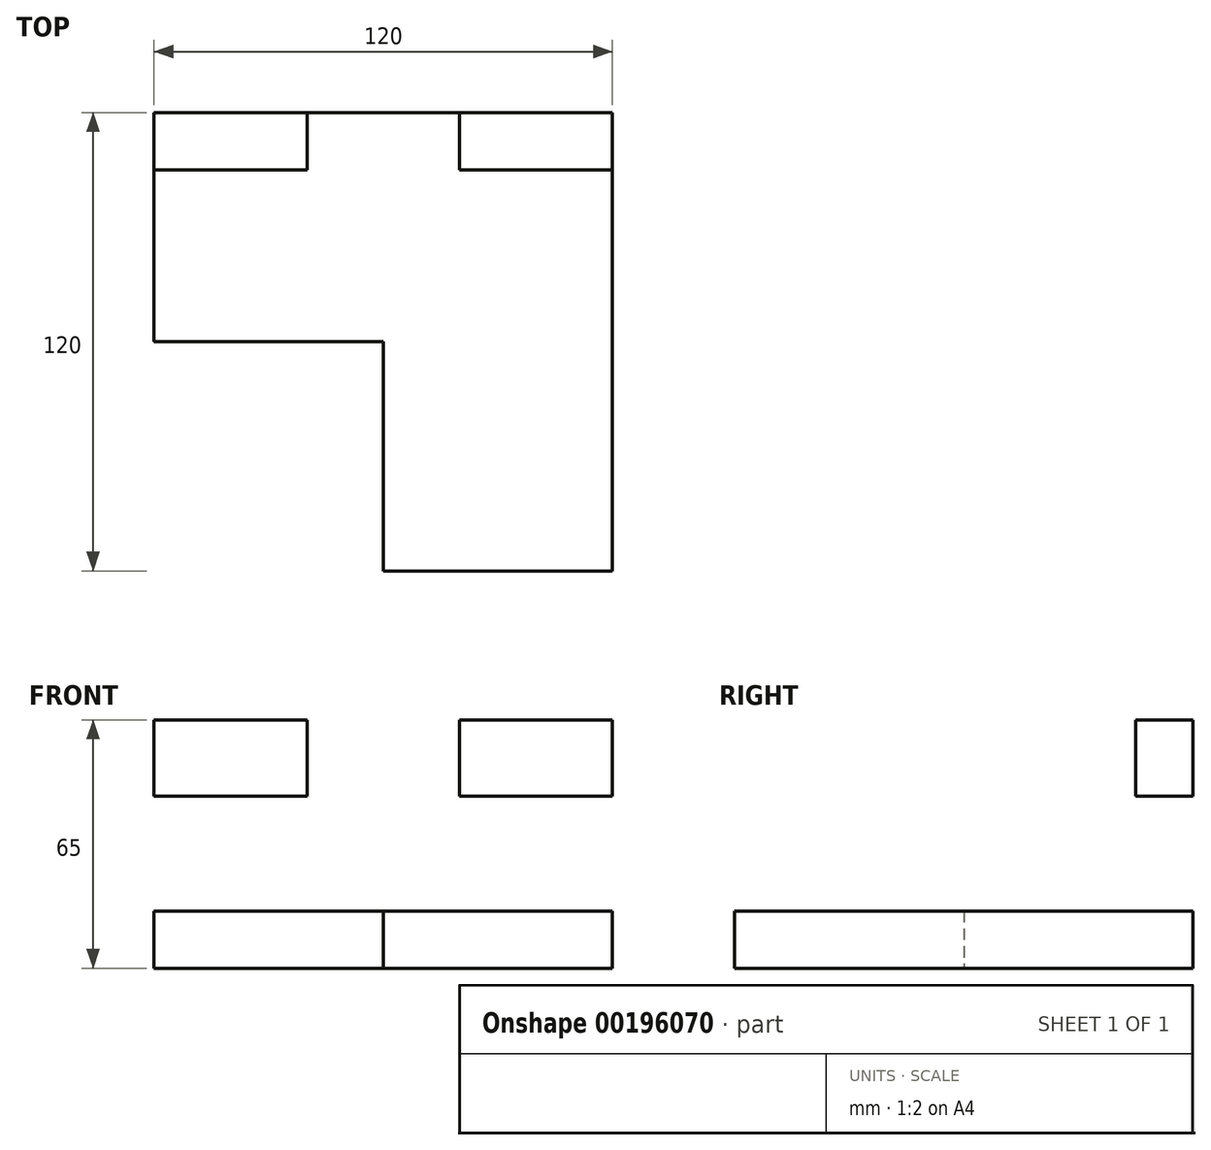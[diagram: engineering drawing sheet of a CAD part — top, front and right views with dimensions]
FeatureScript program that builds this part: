
annotation { "Feature Type Name" : "Feature", "Feature Type Description" : "" }
export const myFeature = defineFeature(function(context is Context, id is Id, definition is map)
    precondition{}
    {
        {
            var Q0;
            Q0=qCreatedBy(makeId("Top.planeOp"),FACE);
            var sketch = newSketch(context, id + "F0", { "sketchPlane" : qUnion([Q0])});
            skLineSegment(sketch, "E0.bottom", {"start": v(0, 0) * mm, "end": v(-120, 0) * mm});
            skLineSegment(sketch, "E0.top", {"start": v(0, -120) * mm, "end": v(-120, -120) * mm});
            skLineSegment(sketch, "E0.left", {"start": v(0, 0) * mm, "end": v(0, -120) * mm});
            skLineSegment(sketch, "E0.right", {"start": v(-120, 0) * mm, "end": v(-120, -120) * mm});
            skLineSegment(sketch, "E1.bottom", {"start": v(-120, -120) * mm, "end": v(-60, -120) * mm});
            skLineSegment(sketch, "E1.top", {"start": v(-120, -60) * mm, "end": v(-60, -60) * mm});
            skLineSegment(sketch, "E1.left", {"start": v(-120, -120) * mm, "end": v(-120, -60) * mm});
            skLineSegment(sketch, "E1.right", {"start": v(-60, -120) * mm, "end": v(-60, -60) * mm});
            skSolve(sketch);
        }
        {
            var Q0;
            Q0=makeQuery(id+"F0.imprint","IMPRINT",FACE,{"disambiguationData":[TD([[makeQuery(id+"F0.imprint","IMPRINT",EDGE,{"derivedFrom":sQuery(id+"F0.wireOp",EDGE,"E0.bottom")}),1.0]])]});
            extrude(context, id + "F1", {"entities" : qUnion([Q0]), "depth" : 15 * mm});
        }
        {
            var Q0;
            Q0=makeQuery(id+"F1.opExtrude","SWEPT_FACE",FACE,{"disambiguationData":[OSD([sQuery(id+"F0.wireOp",EDGE,"E0.bottom")])]});
            var sketch = newSketch(context, id + "F2", { "sketchPlane" : qUnion([Q0])});
            skLineSegment(sketch, "E2.bottom", {"start": v(0, 0) * mm, "end": v(120, 0) * mm});
            skLineSegment(sketch, "E2.top", {"start": v(0, 65) * mm, "end": v(120, 65) * mm});
            skLineSegment(sketch, "E2.left", {"start": v(0, 0) * mm, "end": v(0, 65) * mm});
            skLineSegment(sketch, "E2.right", {"start": v(120, 0) * mm, "end": v(120, 65) * mm});
            skLineSegment(sketch, "E3.bottom", {"start": v(0, 65) * mm, "end": v(40, 65) * mm});
            skLineSegment(sketch, "E3.top", {"start": v(0, 45) * mm, "end": v(40, 45) * mm});
            skLineSegment(sketch, "E3.left", {"start": v(0, 65) * mm, "end": v(0, 45) * mm});
            skLineSegment(sketch, "E3.right", {"start": v(40, 65) * mm, "end": v(40, 45) * mm});
            skLineSegment(sketch, "E4.bottom", {"start": v(120, 65) * mm, "end": v(80, 65) * mm});
            skLineSegment(sketch, "E4.top", {"start": v(120, 45) * mm, "end": v(80, 45) * mm});
            skLineSegment(sketch, "E4.left", {"start": v(120, 65) * mm, "end": v(120, 45) * mm});
            skLineSegment(sketch, "E4.right", {"start": v(80, 65) * mm, "end": v(80, 45) * mm});
            skSolve(sketch);
        }
        {
            var Q0;
            Q0=makeQuery(id+"F2.imprint","IMPRINT",FACE,{"disambiguationData":[TD([[makeQuery(id+"F2.imprint","IMPRINT",EDGE,{"derivedFrom":sQuery(id+"F2.wireOp",EDGE,"E2.top")}),-1.0]])]});
            extrude(context, id + "F3", {"entities" : qUnion([Q0]), "operationType" : NewBodyOperationType.ADD, "oppositeDirection" : true, "depth" : 15 * mm});
        }
    });
